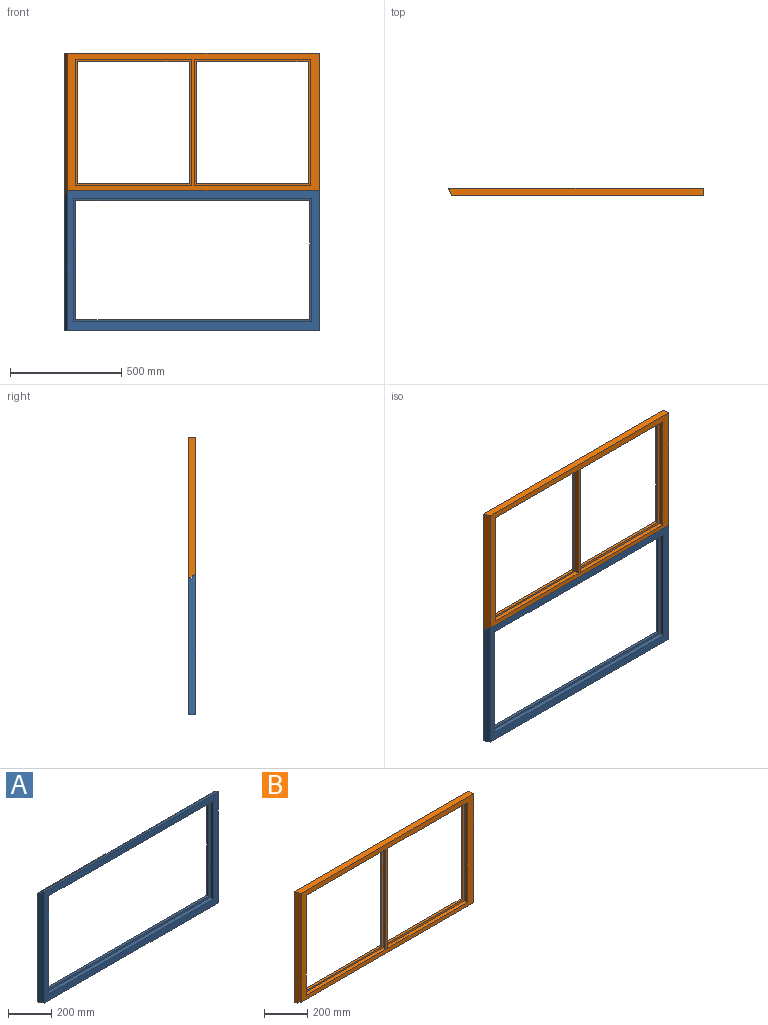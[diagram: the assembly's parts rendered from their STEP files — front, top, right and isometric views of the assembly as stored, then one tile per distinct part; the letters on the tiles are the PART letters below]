
ASSEMBLY  parts=2 mates=1
PART A: 20 faces, bbox 1143x31.8x628.7 mm
  f0: plane 628.65x31.75mm, normal (1,0,0), area 19657.2mm2, adj f1,f9,f15,f16,f17,f18
  f1: plane 1129.97x625.48mm, normal (0,-1,0), area 116544.2mm2, adj f0,f11,f12,f13,f14,f17,f18,f19
  f2: plane 1049.33x12.7mm, normal (0,0,1), area 13326.4mm2, adj f3,f5,f9,f10
  f3: plane 533.4x12.7mm, normal (-1,0,0), area 6774.2mm2, adj f2,f4,f9,f10
  f4: plane 1049.33x12.7mm, normal (0,0,-1), area 13326.4mm2, adj f3,f5,f9,f10
  f5: plane 533.4x12.7mm, normal (1,0,0), area 6774.2mm2, adj f2,f4,f9,f10
  f6: plane 612.54x0.29mm, normal (-1,0,0), area 179mm2, adj f7,f9,f16,f19
  f7: plane 12.7x2.98mm, normal (0,0,-1), area 36.4mm2, adj f6,f8,f9,f18,f19
  f8: plane 2.98x0.3mm, normal (-1,0,0), area 0.4mm2, adj f7,f9,f18
  f9: plane 1143x612.78mm, normal (0,1,0), area 140688.2mm2, adj f0,f2,f3,f4,f5,f6,f7,f8
  f10: plane 1068.38x552.45mm, normal (0,-1,0), area 30513.8mm2, adj f2,f3,f4,f5,f11,f12,f13,f14
  f11: plane 1068.37x19.05mm, normal (0,0,1), area 20352.5mm2, adj f1,f10,f12,f14
  f12: plane 552.45x19.05mm, normal (-1,0,0), area 10524.2mm2, adj f1,f10,f11,f13
  f13: plane 1068.37x19.05mm, normal (0,0,-1), area 20352.5mm2, adj f1,f10,f12,f14
  f14: plane 552.45x19.05mm, normal (1,0,0), area 10524.2mm2, adj f1,f10,f11,f13
  f15: plane 1136.55x9.53mm, normal (0,1,0), area 10825.6mm2, adj f0,f16,f17,f19
  f16: plane 1143x15.88mm, normal (0,0.2,0.98), area 18453.2mm2, adj f0,f6,f9,f15,f19
  f17: plane 1136.55x15.88mm, normal (0,0.2,0.98), area 18346.7mm2, adj f0,f1,f15,f19
  f18: plane 1141.89x31.75mm, normal (0,-0.1,-1), area 36228.7mm2, adj f0,f1,f7,f8,f9,f19
  f19: plane 628.35x31.46mm, normal (-0.92,-0.38,0), area 21082.5mm2, adj f1,f6,f7,f15,f16,f17,f18
PART B: 26 faces, bbox 1143x31.8x630.2 mm
  f0: plane 1129.97x617.54mm, normal (0,-1,0), area 107598.3mm2, adj f1,f9,f12,f13,f14,f15,f18,f19
  f1: plane 630.24x31.75mm, normal (1,0,0), area 19808.4mm2, adj f0,f9,f10,f22,f23,f24
  f2: plane 630.24x0.29mm, normal (-1,0,0), area 184.2mm2, adj f9,f10,f22,f25
  f3: plane 1035.05x12.7mm, normal (0,0,1), area 12892.7mm2, adj f5,f6,f7,f8,f10,f11,f16,f17
  f4: plane 1035.05x12.7mm, normal (0,0,-1), area 12892.7mm2, adj f5,f6,f7,f8,f10,f11,f16,f17
  f5: plane 547.69x12.7mm, normal (-1,0,0), area 6955.6mm2, adj f3,f4,f10,f16
  f6: plane 547.69x12.7mm, normal (1,0,0), area 6955.6mm2, adj f3,f4,f10,f17
  f7: plane 547.69x7.95mm, normal (-1,0,0), area 4354.2mm2, adj f3,f4,f11,f17
  f8: plane 547.69x7.95mm, normal (1,0,0), area 4354.2mm2, adj f3,f4,f11,f16
  f9: plane 1143x31.75mm, normal (0,0,1), area 36085.3mm2, adj f0,f1,f2,f10,f25
  f10: plane 1143x630.24mm, normal (0,1,0), area 153477.5mm2, adj f1,f2,f3,f4,f5,f6,f9,f22
  f11: plane 547.69x31.75mm, normal (0,1,0), area 17389.1mm2, adj f3,f4,f7,f8
  f12: plane 520.7x19.05mm, normal (0,0,-1), area 9919.3mm2, adj f0,f13,f15,f16
  f13: plane 566.74x19.05mm, normal (1,0,0), area 10796.3mm2, adj f0,f12,f14,f16
  f14: plane 520.7x19.05mm, normal (0,0,1), area 9919.3mm2, adj f0,f13,f15,f16
  f15: plane 566.74x19.05mm, normal (-1,0,0), area 10796.3mm2, adj f0,f12,f14,f16
  f16: plane 566.74x520.7mm, normal (0,-1,0), area 20352.8mm2, adj f3,f4,f5,f8,f12,f13,f14,f15
  f17: plane 566.74x520.7mm, normal (0,-1,0), area 20352.8mm2, adj f3,f4,f6,f7,f18,f19,f20,f21
  f18: plane 520.7x19.05mm, normal (0,0,-1), area 9919.3mm2, adj f0,f17,f19,f21
  f19: plane 566.74x19.05mm, normal (1,0,0), area 10796.3mm2, adj f0,f17,f18,f20
  f20: plane 520.7x19.05mm, normal (0,0,1), area 9919.3mm2, adj f0,f17,f19,f21
  f21: plane 566.74x19.05mm, normal (-1,0,0), area 10796.3mm2, adj f0,f17,f18,f20
  f22: plane 1143x15.88mm, normal (0,-0.2,-0.98), area 18453.2mm2, adj f1,f2,f10,f23,f25
  f23: plane 1136.55x6.35mm, normal (0,-1,0), area 7217.1mm2, adj f1,f22,f24,f25
  f24: plane 1136.55x15.88mm, normal (0,-0.2,-0.98), area 18346.7mm2, adj f0,f1,f23,f25
  f25: plane 630.18x31.46mm, normal (-0.92,-0.38,0), area 21241.1mm2, adj f0,f2,f9,f22,f23,f24
PLACE A t=(-72.7,-128.31,43.6)mm
PLACE B t=(-331.26,-160.06,679.6)mm
MATE planar B.f1 <-> A.f0  axis (1,0,0) through (237.07,-160.06,374.01)mm
